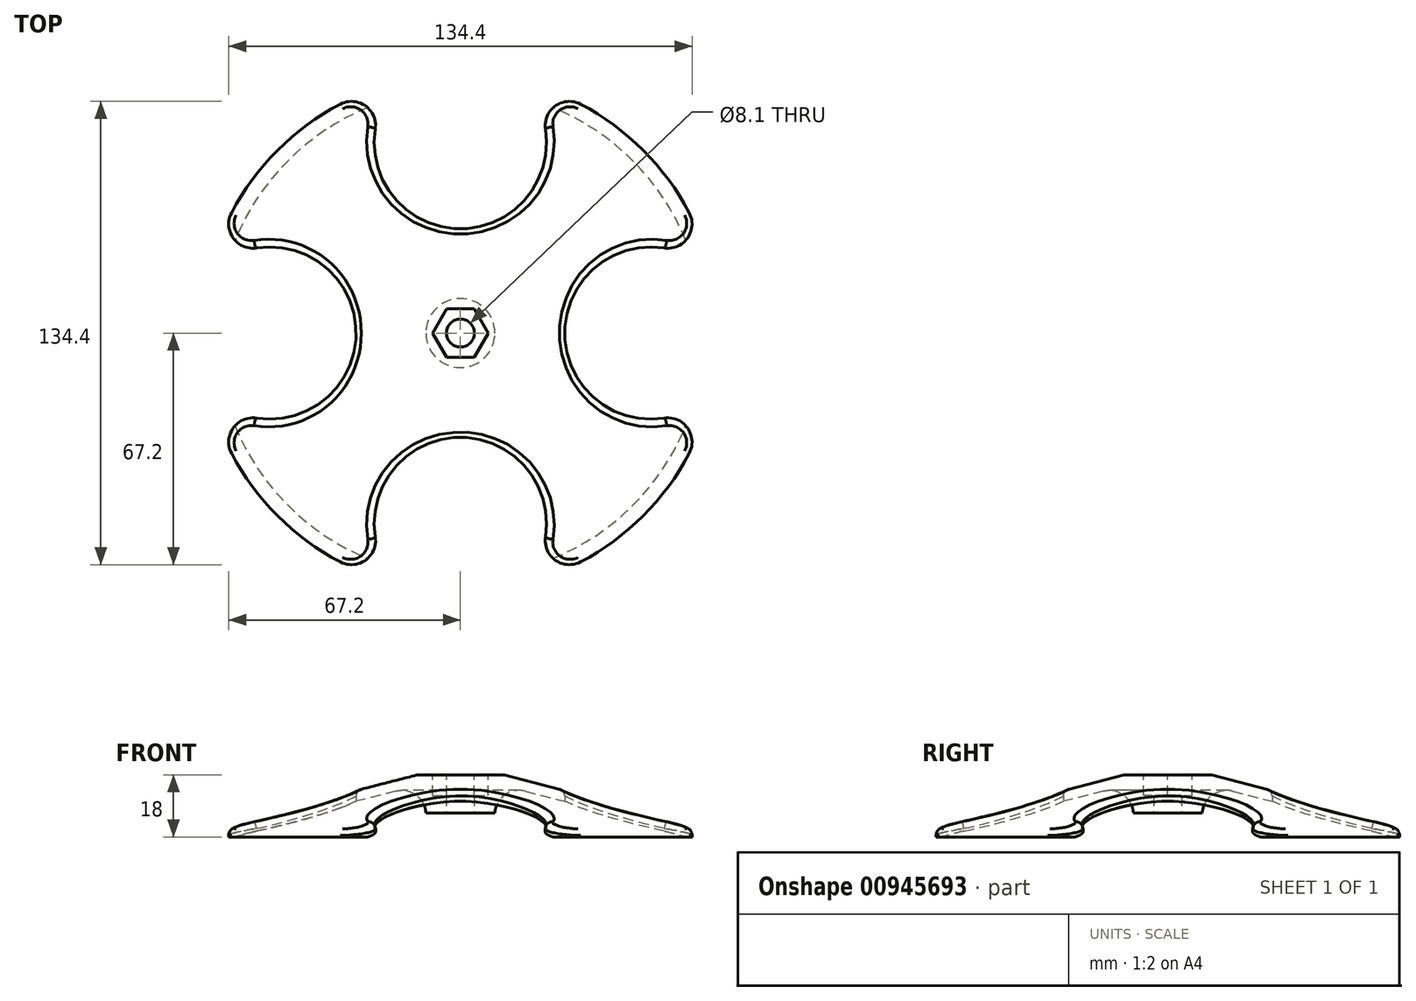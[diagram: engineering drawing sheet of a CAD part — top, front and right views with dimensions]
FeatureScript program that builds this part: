
annotation { "Feature Type Name" : "Feature", "Feature Type Description" : "" }
export const myFeature = defineFeature(function(context is Context, id is Id, definition is map)
    precondition{}
    {
        {
            var Q0;
            Q0=qCreatedBy(makeId("Front.planeOp"),FACE);
            var sketch = newSketch(context, id + "F0", { "sketchPlane" : qUnion([Q0])});
            skLineSegment(sketch, "E0", {"start": v(-75, 0) * mm, "end": v(-75, 2) * mm});
            skLineSegment(sketch, "E1", {"start": v(-75, 2) * mm, "end": v(-12.5, 18) * mm});
            skLineSegment(sketch, "E2", {"start": v(-75, 0) * mm, "end": v(-70.72, 0) * mm});
            skLineSegment(sketch, "E3", {"start": v(-70.72, 0) * mm, "end": v(-10, 15.54) * mm});
            skLineSegment(sketch, "E4", {"start": v(0, 7) * mm, "end": v(0, 18) * mm});
            skLineSegment(sketch, "E5", {"start": v(0, 18) * mm, "end": v(-12.5, 18) * mm});
            skLineSegment(sketch, "E6", {"start": v(-10, 15.54) * mm, "end": v(-10, 7) * mm});
            skLineSegment(sketch, "E7", {"start": v(-10, 7) * mm, "end": v(0, 7) * mm});
            skLineSegment(sketch, "E8", {"start": v(-70.72, 0) * mm, "end": v(0, 0) * mm, "construction": true});
            skSolve(sketch);
        }
        {
            var Q0;
            Q0=makeQuery(id+"F0.imprint","IMPRINT",FACE,{"disambiguationData":[TD([[makeQuery(id+"F0.imprint","IMPRINT",EDGE,{"derivedFrom":sQuery(id+"F0.wireOp",EDGE,"E0")}),-1.0]])]});
            var Q1;
            Q1=sQuery(id+"F0.wireOp",EDGE,"E4");
            revolve(context, id + "F1", {"surfaceOperationType" : NewSurfaceOperationType.NEW, "entities" : qUnion([Q0]), "axis" : qUnion([Q1]), "revolveType" : RevolveType.FULL});
        }
        {
            var Q0;
            Q0=qCreatedBy(makeId("Top.planeOp"),FACE);
            var sketch = newSketch(context, id + "F2", { "sketchPlane" : qUnion([Q0])});
            skCircle(sketch, "E9", {"center": v(0, 0) * mm, "radius": 4.05 * mm});
            skSolve(sketch);
        }
        {
            var Q0;
            Q0 = qSketchRegion(id + "F2", true);
            extrude(context, id + "F3", {"entities" : qUnion([Q0]), "operationType" : NewBodyOperationType.REMOVE, "oppositeDirection" : true, "depth" : -30 * mm, "offsetDistance" : 25 * mm});
        }
        {
            var Q0;
            Q0=qCreatedBy(makeId("Top.planeOp"),FACE);
            var sketch = newSketch(context, id + "F4", { "sketchPlane" : qUnion([Q0])});
            skCircle(sketch, "E10", {"center": v(0, 55.25) * mm, "radius": 25 * mm});
            skCircle(sketch, "E11.1.0", {"center": v(-55.25, 0) * mm, "radius": 25 * mm});
            skCircle(sketch, "E11.2.0", {"center": v(0, -55.25) * mm, "radius": 25 * mm});
            skCircle(sketch, "E11.3.0", {"center": v(55.25, 0) * mm, "radius": 25 * mm});
            skPoint(sketch, "E11.center", {"position": v(0, 0) * mm});
            skSolve(sketch);
        }
        {
            var Q0;
            Q0 = qSketchRegion(id + "F4", true);
            extrude(context, id + "F5", {"entities" : qUnion([Q0]), "operationType" : NewBodyOperationType.REMOVE, "oppositeDirection" : true, "depth" : -25 * mm, "offsetDistance" : 25 * mm});
        }
        {
            var Q0;
            Q0=makeQuery(id+"F1.opRevolve","SWEPT_FACE",FACE,{"disambiguationData":[OSD([sQuery(id+"F0.wireOp",EDGE,"E5")])]});
            var sketch = newSketch(context, id + "F6", { "sketchPlane" : qUnion([Q0])});
            skLineSegment(sketch, "E12", {"start": v(-4.04, -7) * mm, "end": v(4.04, -7) * mm});
            skLineSegment(sketch, "E13", {"start": v(0, 0) * mm, "end": v(0, -7) * mm, "construction": true});
            skPoint(sketch, "E14.center", {"position": v(0, 0) * mm});
            skLineSegment(sketch, "E15.1.0", {"start": v(4.04, -7) * mm, "end": v(8.08, 0) * mm});
            skLineSegment(sketch, "E15.2.0", {"start": v(8.08, 0) * mm, "end": v(4.04, 7) * mm});
            skLineSegment(sketch, "E15.3.0", {"start": v(4.04, 7) * mm, "end": v(-4.04, 7) * mm});
            skLineSegment(sketch, "E15.4.0", {"start": v(-4.04, 7) * mm, "end": v(-8.08, 0) * mm});
            skLineSegment(sketch, "E15.5.0", {"start": v(-8.08, 0) * mm, "end": v(-4.04, -7) * mm});
            skSolve(sketch);
        }
        {
            var Q0;
            Q0=makeQuery(id+"F6.imprint","IMPRINT",FACE,{"disambiguationData":[TD([[makeQuery(id+"F6.imprint","IMPRINT",EDGE,{"derivedFrom":sQuery(id+"F6.wireOp",EDGE,"E12")}),1.0]])]});
            extrude(context, id + "F7", {"entities" : qUnion([Q0]), "operationType" : NewBodyOperationType.REMOVE, "oppositeDirection" : true, "depth" : 6 * mm, "offsetDistance" : 25 * mm});
        }
        {
            var Q0;
            Q0=makeQuery(id+"F5.boolean.opBoolean","INTERSECT",EDGE,{"disambiguationData":[OD(0.0)],"derivedFrom":[makeQuery(id+"F1.opRevolve","SWEPT_FACE",FACE,{"disambiguationData":[OSD([sQuery(id+"F0.wireOp",EDGE,"E0")])]}),makeQuery(id+"F5.opExtrude","SWEPT_FACE",FACE,{"disambiguationData":[OSD([sQuery(id+"F4.wireOp",EDGE,"E11.2.0")])]})]});
            var Q1;
            Q1=makeQuery(id+"F5.boolean.opBoolean","INTERSECT",EDGE,{"disambiguationData":[OD(1.0)],"derivedFrom":[makeQuery(id+"F1.opRevolve","SWEPT_FACE",FACE,{"disambiguationData":[OSD([sQuery(id+"F0.wireOp",EDGE,"E0")])]}),makeQuery(id+"F5.opExtrude","SWEPT_FACE",FACE,{"disambiguationData":[OSD([sQuery(id+"F4.wireOp",EDGE,"E11.2.0")])]})]});
            var Q2;
            Q2=makeQuery(id+"F5.boolean.opBoolean","INTERSECT",EDGE,{"disambiguationData":[OD(1.0)],"derivedFrom":[makeQuery(id+"F1.opRevolve","SWEPT_FACE",FACE,{"disambiguationData":[OSD([sQuery(id+"F0.wireOp",EDGE,"E0")])]}),makeQuery(id+"F5.opExtrude","SWEPT_FACE",FACE,{"disambiguationData":[OSD([sQuery(id+"F4.wireOp",EDGE,"E11.1.0")])]})]});
            var Q3;
            Q3=makeQuery(id+"F5.boolean.opBoolean","INTERSECT",EDGE,{"disambiguationData":[OD(0.0)],"derivedFrom":[makeQuery(id+"F1.opRevolve","SWEPT_FACE",FACE,{"disambiguationData":[OSD([sQuery(id+"F0.wireOp",EDGE,"E0")])]}),makeQuery(id+"F5.opExtrude","SWEPT_FACE",FACE,{"disambiguationData":[OSD([sQuery(id+"F4.wireOp",EDGE,"E11.1.0")])]})]});
            var Q4;
            Q4=makeQuery(id+"F5.boolean.opBoolean","INTERSECT",EDGE,{"disambiguationData":[OD(0.0)],"derivedFrom":[makeQuery(id+"F1.opRevolve","SWEPT_FACE",FACE,{"disambiguationData":[OSD([sQuery(id+"F0.wireOp",EDGE,"E0")])]}),makeQuery(id+"F5.opExtrude","SWEPT_FACE",FACE,{"disambiguationData":[OSD([sQuery(id+"F4.wireOp",EDGE,"E10")])]})]});
            var Q5;
            Q5=makeQuery(id+"F5.boolean.opBoolean","INTERSECT",EDGE,{"disambiguationData":[OD(1.0)],"derivedFrom":[makeQuery(id+"F1.opRevolve","SWEPT_FACE",FACE,{"disambiguationData":[OSD([sQuery(id+"F0.wireOp",EDGE,"E0")])]}),makeQuery(id+"F5.opExtrude","SWEPT_FACE",FACE,{"disambiguationData":[OSD([sQuery(id+"F4.wireOp",EDGE,"E10")])]})]});
            var Q6;
            Q6=makeQuery(id+"F5.boolean.opBoolean","INTERSECT",EDGE,{"disambiguationData":[OD(0.0)],"derivedFrom":[makeQuery(id+"F1.opRevolve","SWEPT_FACE",FACE,{"disambiguationData":[OSD([sQuery(id+"F0.wireOp",EDGE,"E0")])]}),makeQuery(id+"F5.opExtrude","SWEPT_FACE",FACE,{"disambiguationData":[OSD([sQuery(id+"F4.wireOp",EDGE,"E11.3.0")])]})]});
            var Q7;
            Q7=makeQuery(id+"F5.boolean.opBoolean","INTERSECT",EDGE,{"disambiguationData":[OD(1.0)],"derivedFrom":[makeQuery(id+"F1.opRevolve","SWEPT_FACE",FACE,{"disambiguationData":[OSD([sQuery(id+"F0.wireOp",EDGE,"E0")])]}),makeQuery(id+"F5.opExtrude","SWEPT_FACE",FACE,{"disambiguationData":[OSD([sQuery(id+"F4.wireOp",EDGE,"E11.3.0")])]})]});
            var Q8;
            Q8=makeQuery(id+"F1.opRevolve","SWEPT_EDGE",EDGE,{"disambiguationData":[OSD([sQuery(id+"F0.wireOp",EDGE,"E3"),sQuery(id+"F0.wireOp",EDGE,"E6")])]});
            fillet(context, id + "F8", {"entities" : qUnion([Q0, Q1, Q2, Q3, Q4, Q5, Q6, Q7, Q8]), "radius" : 7 * mm, "tangentPropagation" : true, "allowEdgeOverflow" : false});
        }
        {
            var Q0;
            Q0=makeQuery(id+"F1.opRevolve","SWEPT_FACE",FACE,{"disambiguationData":[OSD([sQuery(id+"F0.wireOp",EDGE,"E1")])]});
            fillet(context, id + "F9", {"entities" : qUnion([Q0]), "radius" : 2 * mm, "tangentPropagation" : true, "allowEdgeOverflow" : false});
        }
    });
